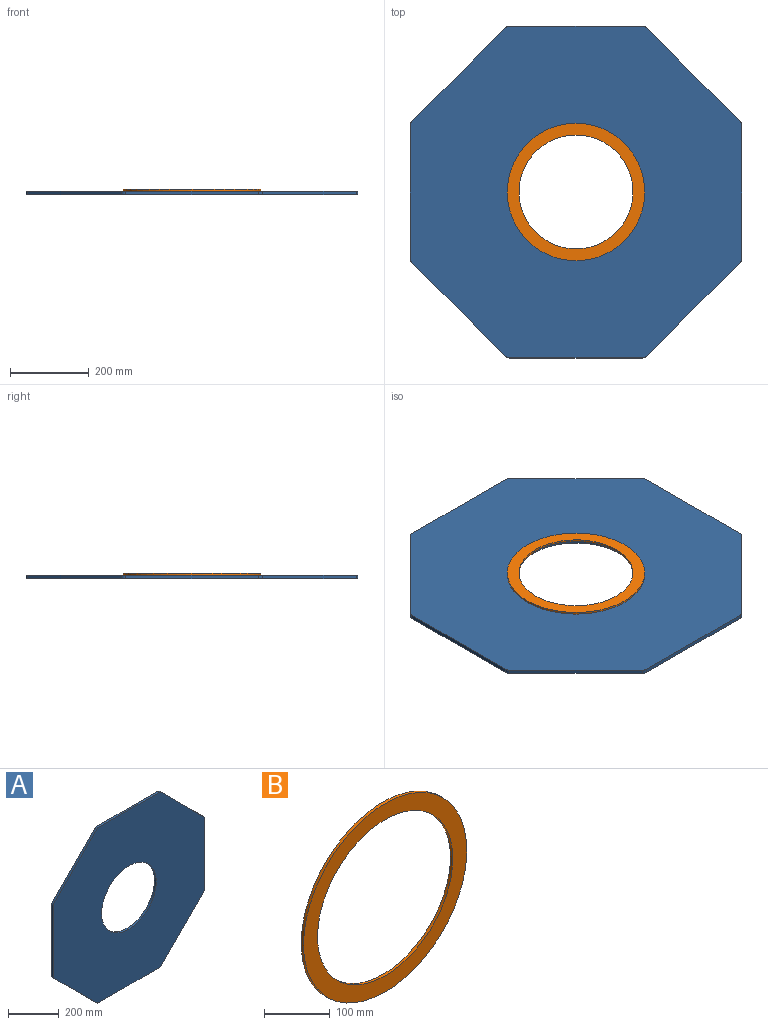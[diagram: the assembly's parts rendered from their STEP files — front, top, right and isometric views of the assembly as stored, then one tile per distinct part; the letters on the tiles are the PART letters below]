
ASSEMBLY  parts=2 mates=1
PART A: 19 faces, bbox 845x10x845 mm
  f0: plane 337.57x10mm, normal (0,0,1), area 3375.7mm2, adj f9,f10,f11,f18
  f1: plane 238.7x238.7mm, normal (-0.71,0,0.71), area 3375.7mm2, adj f9,f10,f11,f12
  f2: plane 337.57x10mm, normal (-1,0,0), area 3375.7mm2, adj f9,f10,f12,f13
  f3: plane 238.7x238.7mm, normal (-0.71,0,-0.71), area 3375.7mm2, adj f9,f10,f13,f14
  f4: plane 337.57x10mm, normal (0,0,-1), area 3375.7mm2, adj f9,f10,f14,f15
  f5: plane 238.7x238.7mm, normal (0.71,0,-0.71), area 3375.7mm2, adj f9,f10,f15,f16
  f6: plane 337.57x10mm, normal (1,0,0), area 3375.7mm2, adj f9,f10,f16,f17
  f7: plane 238.7x238.7mm, normal (0.71,0,0.71), area 3375.7mm2, adj f9,f10,f17,f18
  f8: cylinder r=152.5mm len=305mm, axis (0,1,0), area 9581.9mm2, adj f9,f10
  f9: plane 844.97x844.97mm, normal (0,-1,0), area 518381.9mm2, adj f0,f1,f2,f3,f4,f5,f6,f7
  f10: plane 844.97x844.97mm, normal (0,1,0), area 518381.9mm2, adj f0,f1,f2,f3,f4,f5,f6,f7
  f11: cylinder r=15mm len=10.61mm, axis (0,1,0), area 117.8mm2, adj f0,f1,f9,f10
  f12: cylinder r=15mm len=10.61mm, axis (0,1,0), area 117.8mm2, adj f1,f2,f9,f10
  f13: cylinder r=15mm len=10.61mm, axis (0,1,0), area 117.8mm2, adj f2,f3,f9,f10
  f14: cylinder r=15mm len=10.61mm, axis (0,1,0), area 117.8mm2, adj f3,f4,f9,f10
  f15: cylinder r=15mm len=10.61mm, axis (0,1,0), area 117.8mm2, adj f4,f5,f9,f10
  f16: cylinder r=15mm len=10.61mm, axis (0,1,0), area 117.8mm2, adj f5,f6,f9,f10
  f17: cylinder r=15mm len=10.61mm, axis (0,1,0), area 117.8mm2, adj f6,f7,f9,f10
  f18: cylinder r=15mm len=10.61mm, axis (0,1,0), area 117.8mm2, adj f0,f7,f9,f10
PART B: 4 faces, bbox 350x5x350 mm
  f0: cylinder r=145mm len=290mm, axis (0,1,0), area 4555.3mm2, adj f2,f3
  f1: cylinder r=175mm len=350mm, axis (0,1,0), area 5497.8mm2, adj f2,f3
  f2: plane 350x350mm, normal (0,-1,0), area 30159.3mm2, adj f0,f1
  f3: plane 350x350mm, normal (0,1,0), area 30159.3mm2, adj f0,f1
PLACE A rot(axis=(-1,0,0),90deg) t=(0,0,-10)mm
PLACE B rot(axis=(1,0,0),90deg) t=(0,0,5)mm
MATE fastened B.f1 <-> A.f8  axis (0,0,-1) through (0,0,0)mm
